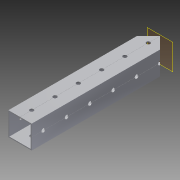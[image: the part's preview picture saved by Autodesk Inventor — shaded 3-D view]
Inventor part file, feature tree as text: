
AUTODESK INVENTOR PART (.ipt)
format: ipt  version: 2014 (Build 180170000, 170)  size: 1,252,352 bytes
history: native  units: in
note: dims shown in document units (in); Inventor stores cm internally (conversion verified against a paired STEP export)
features: extrude x3, sketch x2, pattern_circular x1, other x1, plane x1, imported_body x1
ambient origin geometry x8: Origin, YZ Plane, XZ Plane, XY Plane, X Axis, Y Axis, Z Axis, Center Point
bodies: Body1 (feature_tree)
feature tree (9):
  pattern_circular  "CirPattern2"
  other  "217-3426-STEP1"
  plane  "Work Plane1"
  extrude  "Extrusion1"  Depth=393.7008in TaperAngle=0.0deg
  extrude  "Extrusion2"  Depth=1.0in TaperAngle=0.0deg
  extrude  "Extrusion3"  Depth=1.0in
  imported_body  "Base1"
  sketch  "Sketch1"  dims[d0=-6.0in d1=393.7008in d2=0.0in]
  sketch  "Sketch3"  dims[d3=0.5in d4=39.3701in d5=0.0in d8=0.5in d9=1.0in d10=0.0in d12=45.0deg d13=30.0deg d14=30.0deg d15=1.0in]
